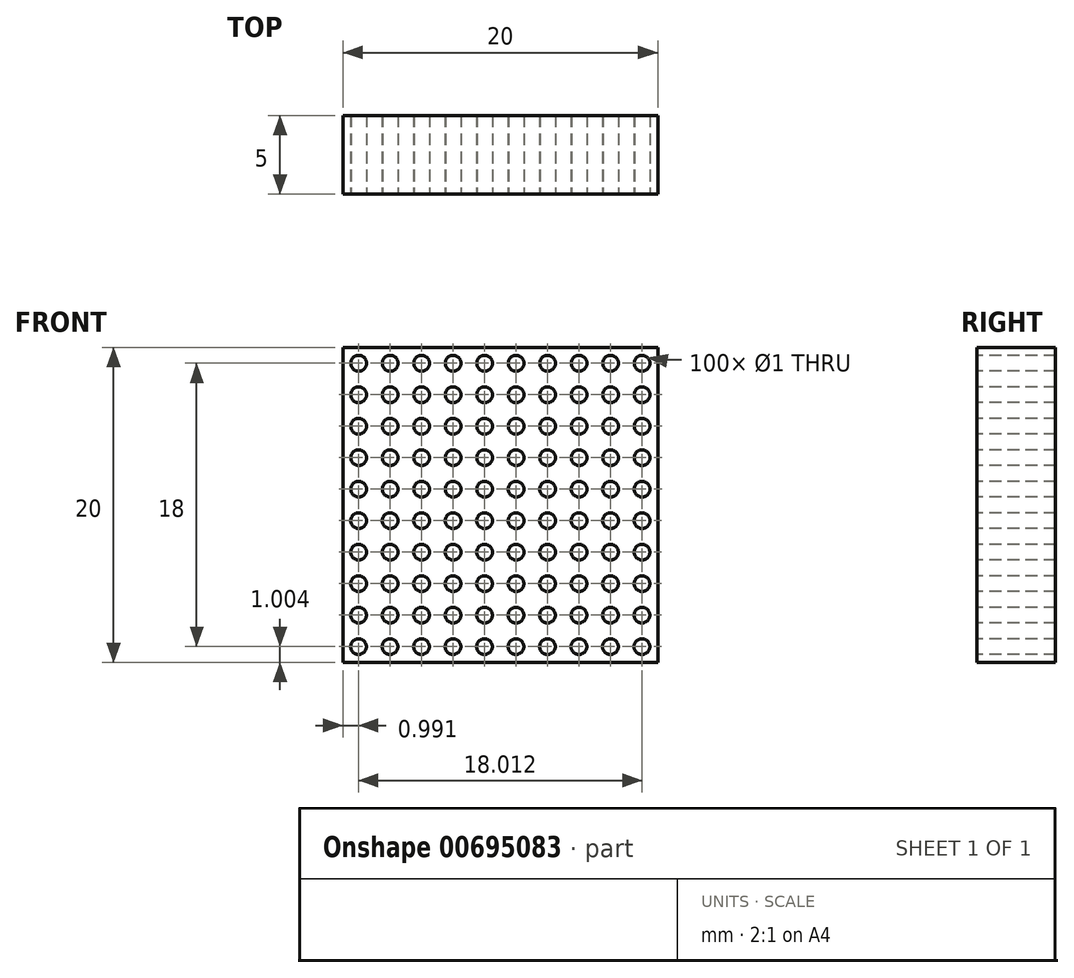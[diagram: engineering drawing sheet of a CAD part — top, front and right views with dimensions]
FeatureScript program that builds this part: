
annotation { "Feature Type Name" : "Feature", "Feature Type Description" : "" }
export const myFeature = defineFeature(function(context is Context, id is Id, definition is map)
    precondition{}
    {
        {
            var Q0;
            Q0=qCreatedBy(makeId("Front.planeOp"),FACE);
            var sketch = newSketch(context, id + "F0", { "sketchPlane" : qUnion([Q0])});
            skLineSegment(sketch, "E0.bottom", {"start": v(-64.18, -11.82) * mm, "end": v(-44.18, -11.82) * mm});
            skLineSegment(sketch, "E0.top", {"start": v(-64.18, -31.82) * mm, "end": v(-44.18, -31.82) * mm});
            skLineSegment(sketch, "E0.left", {"start": v(-64.18, -11.82) * mm, "end": v(-64.18, -31.82) * mm});
            skLineSegment(sketch, "E0.right", {"start": v(-44.18, -11.82) * mm, "end": v(-44.18, -31.82) * mm});
            skSolve(sketch);
        }
        {
            var Q0;
            Q0=makeQuery(id+"F0.imprint","IMPRINT",FACE,{"disambiguationData":[TD([[makeQuery(id+"F0.imprint","IMPRINT",EDGE,{"derivedFrom":sQuery(id+"F0.wireOp",EDGE,"E0.bottom")}),-1.0]])]});
            extrude(context, id + "F1", {"entities" : qUnion([Q0]), "depth" : 5 * mm, "offsetDistance" : 25 * mm});
        }
        {
            var Q0;
            Q0=makeQuery(id+"F1.opExtrude","CAP_FACE",FACE,{"disambiguationData":[OSD([sQuery(id+"F0.wireOp",EDGE,"E0.bottom"),sQuery(id+"F0.wireOp",EDGE,"E0.top"),sQuery(id+"F0.wireOp",EDGE,"E0.left"),sQuery(id+"F0.wireOp",EDGE,"E0.right")])],"isStart":false});
            var sketch = newSketch(context, id + "F2", { "sketchPlane" : qUnion([Q0])});
            skCircle(sketch, "E1", {"center": v(-63.18, -12.82) * mm, "radius": 0.5 * mm});
            skCircle(sketch, "E2.1.0.0", {"center": v(-61.18, -12.82) * mm, "radius": 0.5 * mm});
            skCircle(sketch, "E2.2.0.0", {"center": v(-59.18, -12.82) * mm, "radius": 0.5 * mm});
            skCircle(sketch, "E2.3.0.0", {"center": v(-57.18, -12.82) * mm, "radius": 0.5 * mm});
            skCircle(sketch, "E2.4.0.0", {"center": v(-55.18, -12.82) * mm, "radius": 0.5 * mm});
            skCircle(sketch, "E2.5.0.0", {"center": v(-53.18, -12.82) * mm, "radius": 0.5 * mm});
            skCircle(sketch, "E2.6.0.0", {"center": v(-51.18, -12.82) * mm, "radius": 0.5 * mm});
            skCircle(sketch, "E2.7.0.0", {"center": v(-49.18, -12.82) * mm, "radius": 0.5 * mm});
            skCircle(sketch, "E2.8.0.0", {"center": v(-47.18, -12.82) * mm, "radius": 0.5 * mm});
            skCircle(sketch, "E2.9.0.0", {"center": v(-45.18, -12.82) * mm, "radius": 0.5 * mm});
            skLineSegment(sketch, "E2.direction1", {"start": v(-63.18, -12.82) * mm, "end": v(-61.18, -12.82) * mm, "construction": true});
            skCircle(sketch, "E3.1.0.0", {"center": v(-47.18, -14.82) * mm, "radius": 0.5 * mm});
            skCircle(sketch, "E3.1.0.1", {"center": v(-45.18, -14.82) * mm, "radius": 0.5 * mm});
            skCircle(sketch, "E3.1.0.2", {"center": v(-49.18, -14.82) * mm, "radius": 0.5 * mm});
            skCircle(sketch, "E3.1.0.3", {"center": v(-51.18, -14.82) * mm, "radius": 0.5 * mm});
            skCircle(sketch, "E3.1.0.4", {"center": v(-53.18, -14.82) * mm, "radius": 0.5 * mm});
            skCircle(sketch, "E3.1.0.5", {"center": v(-55.18, -14.82) * mm, "radius": 0.5 * mm});
            skCircle(sketch, "E3.1.0.6", {"center": v(-57.18, -14.82) * mm, "radius": 0.5 * mm});
            skCircle(sketch, "E3.1.0.7", {"center": v(-59.18, -14.82) * mm, "radius": 0.5 * mm});
            skLineSegment(sketch, "E3.1.0.8", {"start": v(-63.18, -14.82) * mm, "end": v(-61.18, -14.82) * mm, "construction": true});
            skCircle(sketch, "E3.1.0.9", {"center": v(-61.18, -14.82) * mm, "radius": 0.5 * mm});
            skCircle(sketch, "E3.1.0.10", {"center": v(-63.18, -14.82) * mm, "radius": 0.5 * mm});
            skCircle(sketch, "E3.2.0.0", {"center": v(-47.18, -16.82) * mm, "radius": 0.5 * mm});
            skCircle(sketch, "E3.2.0.1", {"center": v(-45.18, -16.82) * mm, "radius": 0.5 * mm});
            skCircle(sketch, "E3.2.0.2", {"center": v(-49.18, -16.82) * mm, "radius": 0.5 * mm});
            skCircle(sketch, "E3.2.0.3", {"center": v(-51.18, -16.82) * mm, "radius": 0.5 * mm});
            skCircle(sketch, "E3.2.0.4", {"center": v(-53.18, -16.82) * mm, "radius": 0.5 * mm});
            skCircle(sketch, "E3.2.0.5", {"center": v(-55.18, -16.82) * mm, "radius": 0.5 * mm});
            skCircle(sketch, "E3.2.0.6", {"center": v(-57.18, -16.82) * mm, "radius": 0.5 * mm});
            skCircle(sketch, "E3.2.0.7", {"center": v(-59.18, -16.82) * mm, "radius": 0.5 * mm});
            skLineSegment(sketch, "E3.2.0.8", {"start": v(-63.18, -16.82) * mm, "end": v(-61.18, -16.82) * mm, "construction": true});
            skCircle(sketch, "E3.2.0.9", {"center": v(-61.18, -16.82) * mm, "radius": 0.5 * mm});
            skCircle(sketch, "E3.2.0.10", {"center": v(-63.18, -16.82) * mm, "radius": 0.5 * mm});
            skCircle(sketch, "E3.3.0.0", {"center": v(-47.18, -18.82) * mm, "radius": 0.5 * mm});
            skCircle(sketch, "E3.3.0.1", {"center": v(-45.18, -18.82) * mm, "radius": 0.5 * mm});
            skCircle(sketch, "E3.3.0.2", {"center": v(-49.18, -18.82) * mm, "radius": 0.5 * mm});
            skCircle(sketch, "E3.3.0.3", {"center": v(-51.18, -18.82) * mm, "radius": 0.5 * mm});
            skCircle(sketch, "E3.3.0.4", {"center": v(-53.18, -18.82) * mm, "radius": 0.5 * mm});
            skCircle(sketch, "E3.3.0.5", {"center": v(-55.18, -18.82) * mm, "radius": 0.5 * mm});
            skCircle(sketch, "E3.3.0.6", {"center": v(-57.18, -18.82) * mm, "radius": 0.5 * mm});
            skCircle(sketch, "E3.3.0.7", {"center": v(-59.18, -18.82) * mm, "radius": 0.5 * mm});
            skLineSegment(sketch, "E3.3.0.8", {"start": v(-63.18, -18.82) * mm, "end": v(-61.18, -18.82) * mm, "construction": true});
            skCircle(sketch, "E3.3.0.9", {"center": v(-61.18, -18.82) * mm, "radius": 0.5 * mm});
            skCircle(sketch, "E3.3.0.10", {"center": v(-63.18, -18.82) * mm, "radius": 0.5 * mm});
            skCircle(sketch, "E3.4.0.0", {"center": v(-47.18, -20.82) * mm, "radius": 0.5 * mm});
            skCircle(sketch, "E3.4.0.1", {"center": v(-45.18, -20.82) * mm, "radius": 0.5 * mm});
            skCircle(sketch, "E3.4.0.2", {"center": v(-49.18, -20.82) * mm, "radius": 0.5 * mm});
            skCircle(sketch, "E3.4.0.3", {"center": v(-51.18, -20.82) * mm, "radius": 0.5 * mm});
            skCircle(sketch, "E3.4.0.4", {"center": v(-53.18, -20.82) * mm, "radius": 0.5 * mm});
            skCircle(sketch, "E3.4.0.5", {"center": v(-55.18, -20.82) * mm, "radius": 0.5 * mm});
            skCircle(sketch, "E3.4.0.6", {"center": v(-57.18, -20.82) * mm, "radius": 0.5 * mm});
            skCircle(sketch, "E3.4.0.7", {"center": v(-59.18, -20.82) * mm, "radius": 0.5 * mm});
            skLineSegment(sketch, "E3.4.0.8", {"start": v(-63.18, -20.82) * mm, "end": v(-61.18, -20.82) * mm, "construction": true});
            skCircle(sketch, "E3.4.0.9", {"center": v(-61.18, -20.82) * mm, "radius": 0.5 * mm});
            skCircle(sketch, "E3.4.0.10", {"center": v(-63.18, -20.82) * mm, "radius": 0.5 * mm});
            skCircle(sketch, "E3.5.0.0", {"center": v(-47.18, -22.82) * mm, "radius": 0.5 * mm});
            skCircle(sketch, "E3.5.0.1", {"center": v(-45.18, -22.82) * mm, "radius": 0.5 * mm});
            skCircle(sketch, "E3.5.0.2", {"center": v(-49.18, -22.82) * mm, "radius": 0.5 * mm});
            skCircle(sketch, "E3.5.0.3", {"center": v(-51.18, -22.82) * mm, "radius": 0.5 * mm});
            skCircle(sketch, "E3.5.0.4", {"center": v(-53.18, -22.82) * mm, "radius": 0.5 * mm});
            skCircle(sketch, "E3.5.0.5", {"center": v(-55.18, -22.82) * mm, "radius": 0.5 * mm});
            skCircle(sketch, "E3.5.0.6", {"center": v(-57.18, -22.82) * mm, "radius": 0.5 * mm});
            skCircle(sketch, "E3.5.0.7", {"center": v(-59.18, -22.82) * mm, "radius": 0.5 * mm});
            skLineSegment(sketch, "E3.5.0.8", {"start": v(-63.18, -22.82) * mm, "end": v(-61.18, -22.82) * mm, "construction": true});
            skCircle(sketch, "E3.5.0.9", {"center": v(-61.18, -22.82) * mm, "radius": 0.5 * mm});
            skCircle(sketch, "E3.5.0.10", {"center": v(-63.18, -22.82) * mm, "radius": 0.5 * mm});
            skCircle(sketch, "E3.6.0.0", {"center": v(-47.18, -24.82) * mm, "radius": 0.5 * mm});
            skCircle(sketch, "E3.6.0.1", {"center": v(-45.18, -24.82) * mm, "radius": 0.5 * mm});
            skCircle(sketch, "E3.6.0.2", {"center": v(-49.18, -24.82) * mm, "radius": 0.5 * mm});
            skCircle(sketch, "E3.6.0.3", {"center": v(-51.18, -24.82) * mm, "radius": 0.5 * mm});
            skCircle(sketch, "E3.6.0.4", {"center": v(-53.18, -24.82) * mm, "radius": 0.5 * mm});
            skCircle(sketch, "E3.6.0.5", {"center": v(-55.18, -24.82) * mm, "radius": 0.5 * mm});
            skCircle(sketch, "E3.6.0.6", {"center": v(-57.18, -24.82) * mm, "radius": 0.5 * mm});
            skCircle(sketch, "E3.6.0.7", {"center": v(-59.18, -24.82) * mm, "radius": 0.5 * mm});
            skLineSegment(sketch, "E3.6.0.8", {"start": v(-63.18, -24.82) * mm, "end": v(-61.18, -24.82) * mm, "construction": true});
            skCircle(sketch, "E3.6.0.9", {"center": v(-61.18, -24.82) * mm, "radius": 0.5 * mm});
            skCircle(sketch, "E3.6.0.10", {"center": v(-63.18, -24.82) * mm, "radius": 0.5 * mm});
            skCircle(sketch, "E3.7.0.0", {"center": v(-47.19, -26.82) * mm, "radius": 0.5 * mm});
            skCircle(sketch, "E3.7.0.1", {"center": v(-45.19, -26.82) * mm, "radius": 0.5 * mm});
            skCircle(sketch, "E3.7.0.2", {"center": v(-49.19, -26.82) * mm, "radius": 0.5 * mm});
            skCircle(sketch, "E3.7.0.3", {"center": v(-51.19, -26.82) * mm, "radius": 0.5 * mm});
            skCircle(sketch, "E3.7.0.4", {"center": v(-53.19, -26.82) * mm, "radius": 0.5 * mm});
            skCircle(sketch, "E3.7.0.5", {"center": v(-55.19, -26.82) * mm, "radius": 0.5 * mm});
            skCircle(sketch, "E3.7.0.6", {"center": v(-57.19, -26.82) * mm, "radius": 0.5 * mm});
            skCircle(sketch, "E3.7.0.7", {"center": v(-59.19, -26.82) * mm, "radius": 0.5 * mm});
            skLineSegment(sketch, "E3.7.0.8", {"start": v(-63.19, -26.82) * mm, "end": v(-61.19, -26.82) * mm, "construction": true});
            skCircle(sketch, "E3.7.0.9", {"center": v(-61.19, -26.82) * mm, "radius": 0.5 * mm});
            skCircle(sketch, "E3.7.0.10", {"center": v(-63.19, -26.82) * mm, "radius": 0.5 * mm});
            skCircle(sketch, "E3.8.0.0", {"center": v(-47.19, -28.82) * mm, "radius": 0.5 * mm});
            skCircle(sketch, "E3.8.0.1", {"center": v(-45.19, -28.82) * mm, "radius": 0.5 * mm});
            skCircle(sketch, "E3.8.0.2", {"center": v(-49.19, -28.82) * mm, "radius": 0.5 * mm});
            skCircle(sketch, "E3.8.0.3", {"center": v(-51.19, -28.82) * mm, "radius": 0.5 * mm});
            skCircle(sketch, "E3.8.0.4", {"center": v(-53.19, -28.82) * mm, "radius": 0.5 * mm});
            skCircle(sketch, "E3.8.0.5", {"center": v(-55.19, -28.82) * mm, "radius": 0.5 * mm});
            skCircle(sketch, "E3.8.0.6", {"center": v(-57.19, -28.82) * mm, "radius": 0.5 * mm});
            skCircle(sketch, "E3.8.0.7", {"center": v(-59.19, -28.82) * mm, "radius": 0.5 * mm});
            skLineSegment(sketch, "E3.8.0.8", {"start": v(-63.19, -28.82) * mm, "end": v(-61.19, -28.82) * mm, "construction": true});
            skCircle(sketch, "E3.8.0.9", {"center": v(-61.19, -28.82) * mm, "radius": 0.5 * mm});
            skCircle(sketch, "E3.8.0.10", {"center": v(-63.19, -28.82) * mm, "radius": 0.5 * mm});
            skCircle(sketch, "E3.9.0.0", {"center": v(-47.19, -30.82) * mm, "radius": 0.5 * mm});
            skCircle(sketch, "E3.9.0.1", {"center": v(-45.19, -30.82) * mm, "radius": 0.5 * mm});
            skCircle(sketch, "E3.9.0.2", {"center": v(-49.19, -30.82) * mm, "radius": 0.5 * mm});
            skCircle(sketch, "E3.9.0.3", {"center": v(-51.19, -30.82) * mm, "radius": 0.5 * mm});
            skCircle(sketch, "E3.9.0.4", {"center": v(-53.19, -30.82) * mm, "radius": 0.5 * mm});
            skCircle(sketch, "E3.9.0.5", {"center": v(-55.19, -30.82) * mm, "radius": 0.5 * mm});
            skCircle(sketch, "E3.9.0.6", {"center": v(-57.19, -30.82) * mm, "radius": 0.5 * mm});
            skCircle(sketch, "E3.9.0.7", {"center": v(-59.19, -30.82) * mm, "radius": 0.5 * mm});
            skLineSegment(sketch, "E3.9.0.8", {"start": v(-63.19, -30.82) * mm, "end": v(-61.19, -30.82) * mm, "construction": true});
            skCircle(sketch, "E3.9.0.9", {"center": v(-61.19, -30.82) * mm, "radius": 0.5 * mm});
            skCircle(sketch, "E3.9.0.10", {"center": v(-63.19, -30.82) * mm, "radius": 0.5 * mm});
            skLineSegment(sketch, "E3.direction1", {"start": v(-63.18, -13.82) * mm, "end": v(-63.18, -15.82) * mm, "construction": true});
            skSolve(sketch);
        }
        {
            var Q0;
            Q0 = qSketchRegion(id + "F2", true);
            extrude(context, id + "F3", {"entities" : qUnion([Q0]), "operationType" : NewBodyOperationType.REMOVE, "oppositeDirection" : true, "depth" : 25 * mm, "offsetDistance" : 25 * mm});
        }
    });
